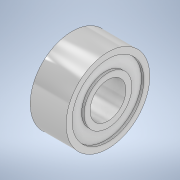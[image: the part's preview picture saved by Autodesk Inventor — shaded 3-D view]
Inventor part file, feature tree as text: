
AUTODESK INVENTOR PART (.ipt)
format: ipt  version: 2020 (Build 240168000, 168)  size: 134,656 bytes
history: native  units: in
note: dims shown in document units (in); Inventor stores cm internally (conversion verified against a paired STEP export)
features: extrude x2, sketch x2, mirror x1
ambient origin geometry x8: Origin, YZ Plane, XZ Plane, XY Plane, X Axis, Y Axis, Z Axis, Center Point
bodies: Solid1 (feature_tree)
feature tree (5):
  extrude  "Extrusion1"  Depth=0.1181in
  extrude  "Extrusion2"  Depth=0.0079in
  mirror  "Mirror1"
  sketch  "Sketch1"  dims[d0=0.1181in d1=0.2756in]
  sketch  "Sketch2"  dims[d2=0.1181in d3=0.0in d4=0.1575in d5=0.2362in d6=0.0079in d7=0.0in]
